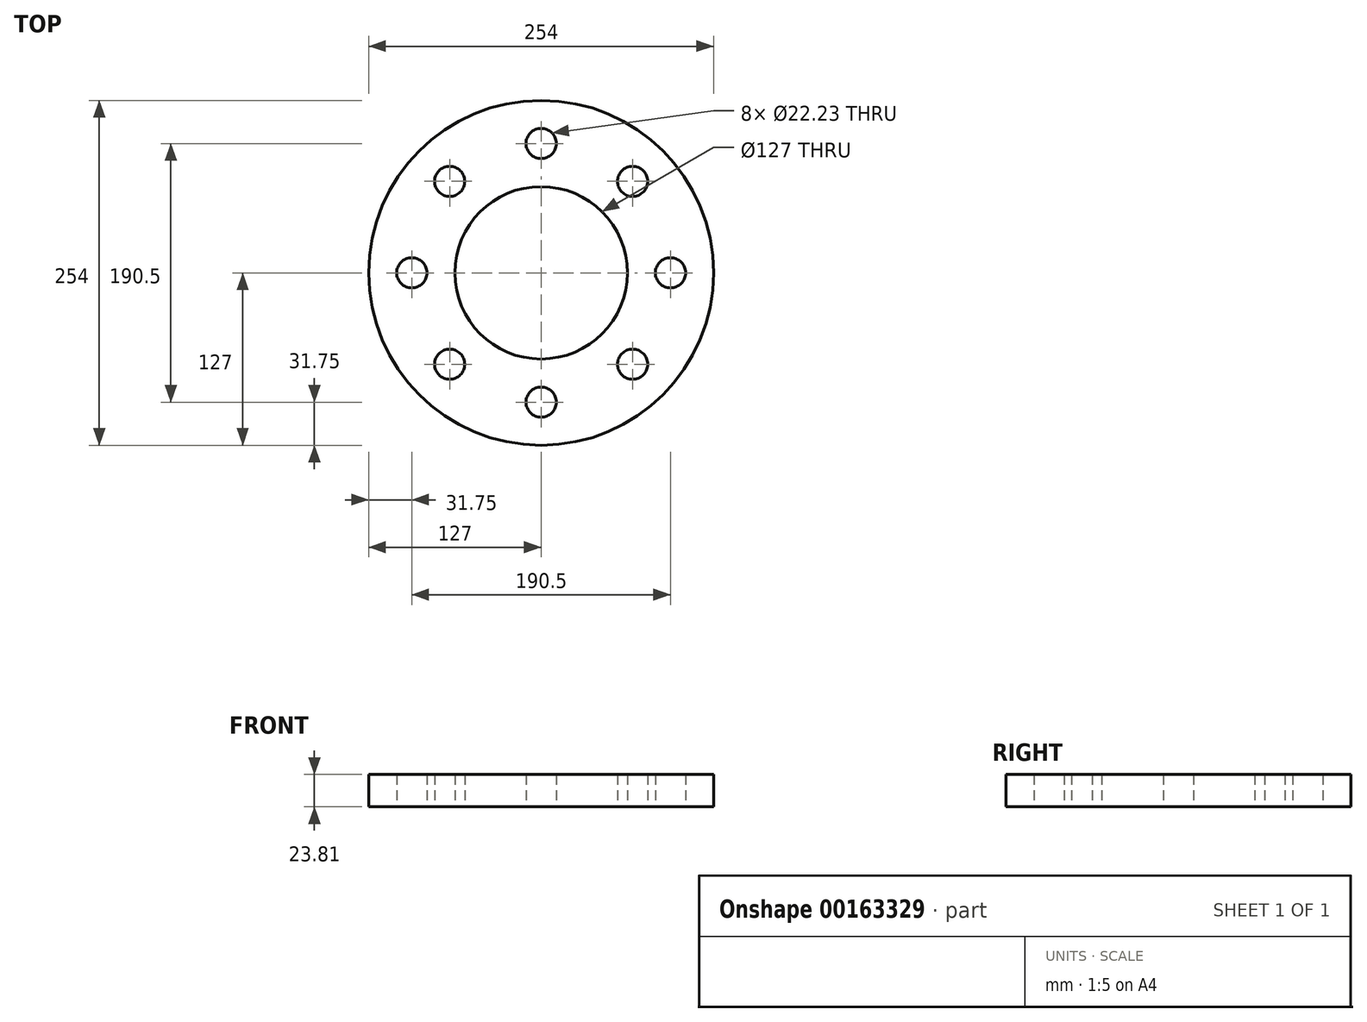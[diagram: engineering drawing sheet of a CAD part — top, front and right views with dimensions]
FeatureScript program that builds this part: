
annotation { "Feature Type Name" : "Feature", "Feature Type Description" : "" }
export const myFeature = defineFeature(function(context is Context, id is Id, definition is map)
    precondition{}
    {
        {
            var Q0;
            Q0=qCreatedBy(makeId("Top.planeOp"),FACE);
            var sketch = newSketch(context, id + "F0", { "sketchPlane" : qUnion([Q0])});
            skCircle(sketch, "E0", {"center": v(0, 0) * mm, "radius": 127 * mm});
            skCircle(sketch, "E1", {"center": v(0, 0) * mm, "radius": 63.5 * mm});
            skCircle(sketch, "E2", {"center": v(0, 95.25) * mm, "radius": 11.11 * mm});
            skCircle(sketch, "E3.1.0", {"center": v(-67.35, 67.35) * mm, "radius": 11.11 * mm});
            skCircle(sketch, "E3.2.0", {"center": v(-95.25, 0) * mm, "radius": 11.11 * mm});
            skCircle(sketch, "E3.3.0", {"center": v(-67.35, -67.35) * mm, "radius": 11.11 * mm});
            skCircle(sketch, "E3.4.0", {"center": v(0, -95.25) * mm, "radius": 11.11 * mm});
            skCircle(sketch, "E3.5.0", {"center": v(67.35, -67.35) * mm, "radius": 11.11 * mm});
            skCircle(sketch, "E3.6.0", {"center": v(95.25, 0) * mm, "radius": 11.11 * mm});
            skCircle(sketch, "E3.7.0", {"center": v(67.35, 67.35) * mm, "radius": 11.11 * mm});
            skSolve(sketch);
        }
        {
            var Q0;
            Q0=makeQuery(id+"F0.imprint","IMPRINT",FACE,{"disambiguationData":[TD([[makeQuery(id+"F0.imprint","IMPRINT",EDGE,{"derivedFrom":sQuery(id+"F0.wireOp",EDGE,"E0")}),1.0]])]});
            extrude(context, id + "F1", {"entities" : qUnion([Q0]), "depth" : 23.8 * mm});
        }
    });
